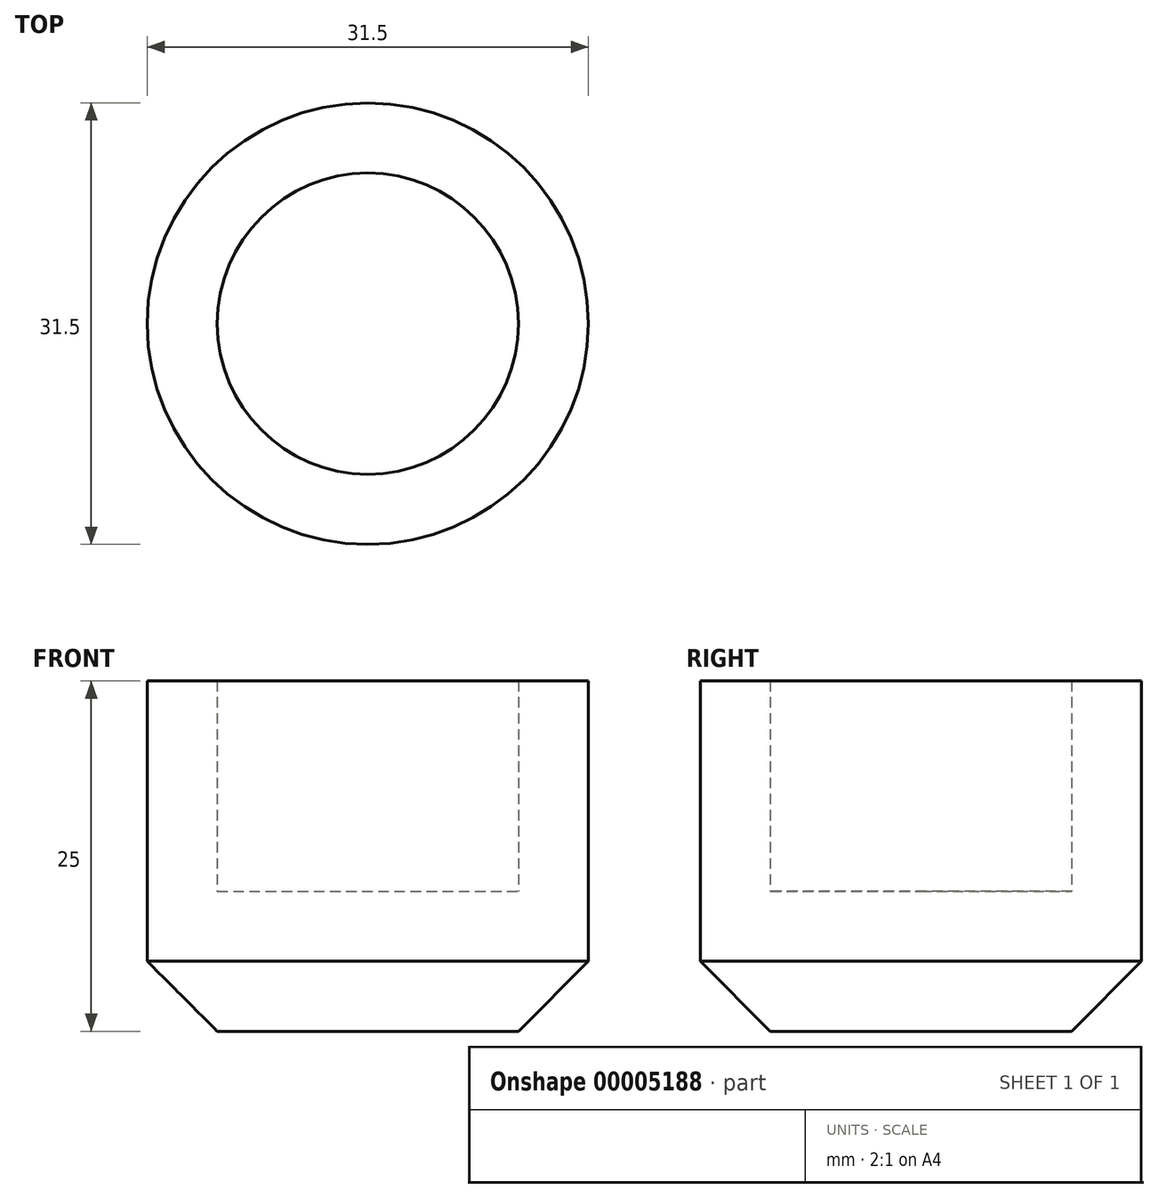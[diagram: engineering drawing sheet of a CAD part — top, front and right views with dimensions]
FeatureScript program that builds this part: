
annotation { "Feature Type Name" : "Feature", "Feature Type Description" : "" }
export const myFeature = defineFeature(function(context is Context, id is Id, definition is map)
    precondition{}
    {
        {
            var Q0;
            Q0=qCreatedBy(makeId("Front.planeOp"),FACE);
            var sketch = newSketch(context, id + "F0", { "sketchPlane" : qUnion([Q0])});
            skLineSegment(sketch, "E0", {"start": v(0, 0) * mm, "end": v(0, 14.32) * mm, "construction": true});
            skLineSegment(sketch, "E1", {"start": v(0, 0) * mm, "end": v(10.75, 0) * mm});
            skLineSegment(sketch, "E2", {"start": v(10.75, 0) * mm, "end": v(15.75, 5) * mm});
            skLineSegment(sketch, "E3", {"start": v(15.75, 5) * mm, "end": v(15.75, 25) * mm});
            skLineSegment(sketch, "E4", {"start": v(15.75, 25) * mm, "end": v(10.75, 25) * mm});
            skLineSegment(sketch, "E5", {"start": v(10.75, 25) * mm, "end": v(10.75, 10) * mm});
            skLineSegment(sketch, "E6", {"start": v(10.75, 10) * mm, "end": v(0, 10) * mm});
            skLineSegment(sketch, "E7", {"start": v(0, 10) * mm, "end": v(0, 0) * mm});
            skSolve(sketch);
        }
        {
            var Q0;
            Q0=makeQuery(id+"F0.imprint","IMPRINT",FACE,{"disambiguationData":[TD([[makeQuery(id+"F0.imprint","IMPRINT",EDGE,{"derivedFrom":sQuery(id+"F0.wireOp",EDGE,"E1")}),1.0]])]});
            var Q1;
            Q1=sQuery(id+"F0.wireOp",EDGE,"E0");
            revolve(context, id + "F1", {"entities" : qUnion([Q0]), "axis" : qUnion([Q1]), "revolveType" : RevolveType.FULL});
        }
    });
